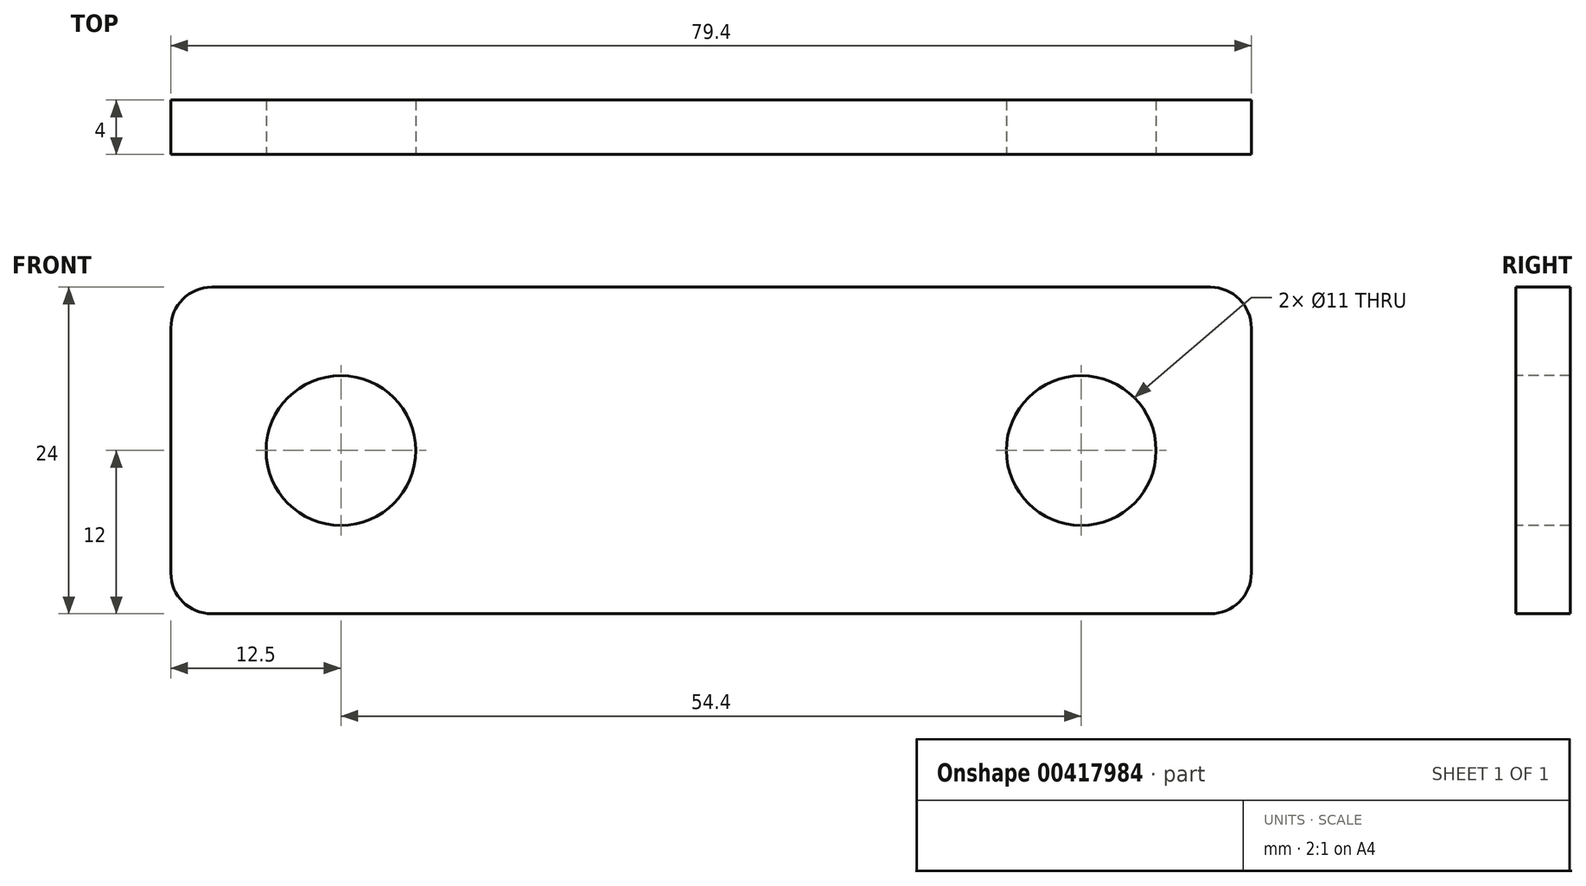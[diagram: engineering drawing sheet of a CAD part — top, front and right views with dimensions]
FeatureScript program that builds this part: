
annotation { "Feature Type Name" : "Feature", "Feature Type Description" : "" }
export const myFeature = defineFeature(function(context is Context, id is Id, definition is map)
    precondition{}
    {
        {
            var Q0;
            Q0=qCreatedBy(makeId("Front.planeOp"),FACE);
            var sketch = newSketch(context, id + "F0", { "sketchPlane" : qUnion([Q0])});
            skLineSegment(sketch, "E0.bottom", {"start": v(39.7, 12) * mm, "end": v(-39.7, 12) * mm});
            skLineSegment(sketch, "E0.top", {"start": v(39.7, -12) * mm, "end": v(-39.7, -12) * mm});
            skLineSegment(sketch, "E0.left", {"start": v(39.7, 12) * mm, "end": v(39.7, -12) * mm});
            skLineSegment(sketch, "E0.right", {"start": v(-39.7, 12) * mm, "end": v(-39.7, -12) * mm});
            skPoint(sketch, "E0.middle", {"position": v(0, 0) * mm});
            skSolve(sketch);
        }
        {
            var Q0;
            Q0=makeQuery(id+"F0.imprint","IMPRINT",FACE,{"disambiguationData":[TD([[makeQuery(id+"F0.imprint","IMPRINT",EDGE,{"derivedFrom":sQuery(id+"F0.wireOp",EDGE,"E0.bottom")}),1.0]])]});
            extrude(context, id + "F1", {"entities" : qUnion([Q0]), "depth" : 4 * mm});
        }
        {
            var Q0;
            Q0=makeQuery(id+"F1.opExtrude","CAP_FACE",FACE,{"disambiguationData":[OSD([sQuery(id+"F0.wireOp",EDGE,"E0.bottom"),sQuery(id+"F0.wireOp",EDGE,"E0.top"),sQuery(id+"F0.wireOp",EDGE,"E0.left"),sQuery(id+"F0.wireOp",EDGE,"E0.right")])],"isStart":false});
            var sketch = newSketch(context, id + "F2", { "sketchPlane" : qUnion([Q0])});
            skCircle(sketch, "E1", {"center": v(-27.2, 0) * mm, "radius": 5.5 * mm});
            skCircle(sketch, "E2", {"center": v(27.2, 0) * mm, "radius": 5.5 * mm});
            skSolve(sketch);
        }
        {
            var Q0;
            Q0=makeQuery(id+"F2.imprint","IMPRINT",FACE,{"disambiguationData":[TD([[makeQuery(id+"F2.imprint","IMPRINT",EDGE,{"derivedFrom":sQuery(id+"F2.wireOp",EDGE,"E1")}),1.0]])]});
            var Q1;
            Q1=makeQuery(id+"F2.imprint","IMPRINT",FACE,{"disambiguationData":[TD([[makeQuery(id+"F2.imprint","IMPRINT",EDGE,{"derivedFrom":sQuery(id+"F2.wireOp",EDGE,"E2")}),1.0]])]});
            extrude(context, id + "F3", {"entities" : qUnion([Q0, Q1]), "operationType" : NewBodyOperationType.REMOVE, "oppositeDirection" : true, "depth" : 25 * mm});
        }
        {
            var Q0;
            Q0=makeQuery(id+"F1.opExtrude","SWEPT_EDGE",EDGE,{"disambiguationData":[OSD([sQuery(id+"F0.wireOp",EDGE,"E0.bottom"),sQuery(id+"F0.wireOp",EDGE,"E0.left")])]});
            var Q1;
            Q1=makeQuery(id+"F1.opExtrude","SWEPT_EDGE",EDGE,{"disambiguationData":[OSD([sQuery(id+"F0.wireOp",EDGE,"E0.top"),sQuery(id+"F0.wireOp",EDGE,"E0.left")])]});
            var Q2;
            Q2=makeQuery(id+"F1.opExtrude","SWEPT_EDGE",EDGE,{"disambiguationData":[OSD([sQuery(id+"F0.wireOp",EDGE,"E0.top"),sQuery(id+"F0.wireOp",EDGE,"E0.right")])]});
            var Q3;
            Q3=makeQuery(id+"F1.opExtrude","SWEPT_EDGE",EDGE,{"disambiguationData":[OSD([sQuery(id+"F0.wireOp",EDGE,"E0.bottom"),sQuery(id+"F0.wireOp",EDGE,"E0.right")])]});
            fillet(context, id + "F4", {"entities" : qUnion([Q0, Q1, Q2, Q3]), "radius" : 3 * mm, "tangentPropagation" : true, "allowEdgeOverflow" : false});
        }
    });
